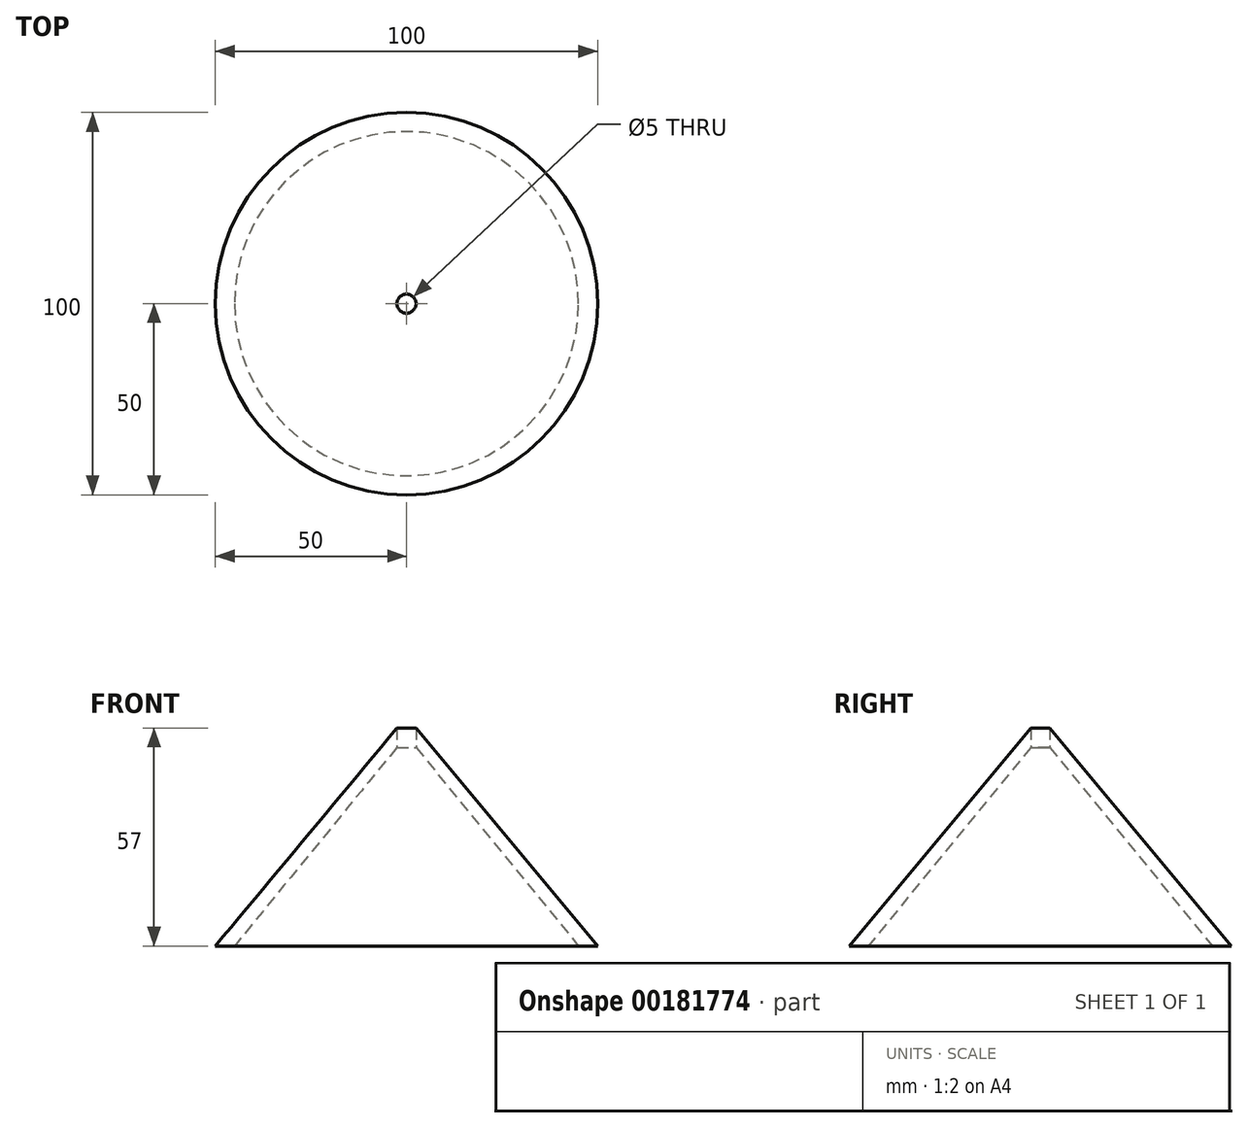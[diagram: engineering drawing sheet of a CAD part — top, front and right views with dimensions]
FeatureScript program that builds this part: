
annotation { "Feature Type Name" : "Feature", "Feature Type Description" : "" }
export const myFeature = defineFeature(function(context is Context, id is Id, definition is map)
    precondition{}
    {
        {
            var Q0;
            Q0=qCreatedBy(makeId("Front.planeOp"),FACE);
            var sketch = newSketch(context, id + "F0", { "sketchPlane" : qUnion([Q0])});
            skLineSegment(sketch, "E0", {"start": v(0, 60) * mm, "end": v(0, 0) * mm});
            skLineSegment(sketch, "E1", {"start": v(0, 0) * mm, "end": v(50, 0) * mm});
            skLineSegment(sketch, "E2", {"start": v(50, 0) * mm, "end": v(0, 60) * mm});
            skSolve(sketch);
        }
        {
            var Q0;
            Q0=makeQuery(id+"F0.imprint","IMPRINT",FACE,{"disambiguationData":[TD([[makeQuery(id+"F0.imprint","IMPRINT",EDGE,{"derivedFrom":sQuery(id+"F0.wireOp",EDGE,"E0")}),1.0]])]});
            var Q1;
            Q1=sQuery(id+"F0.wireOp",EDGE,"E0");
            revolve(context, id + "F1", {"entities" : qUnion([Q0]), "axis" : qUnion([Q1]), "revolveType" : RevolveType.FULL});
        }
        {
            var Q0;
            Q0=qCreatedBy(makeId("Top.planeOp"),FACE);
            var sketch = newSketch(context, id + "F2", { "sketchPlane" : qUnion([Q0])});
            skCircle(sketch, "E3", {"center": v(0, 0) * mm, "radius": 2.5 * mm});
            skSolve(sketch);
        }
        {
            var Q0;
            Q0 = qSketchRegion(id + "F2", true);
            extrude(context, id + "F3", {"entities" : qUnion([Q0]), "operationType" : NewBodyOperationType.REMOVE, "depth" : 60 * mm});
        }
        {
            var Q0;
            Q0=qCreatedBy(makeId("Front.planeOp"),FACE);
            var sketch = newSketch(context, id + "F4", { "sketchPlane" : qUnion([Q0])});
            skLineSegment(sketch, "E4", {"start": v(0, 0) * mm, "end": v(0, 55) * mm});
            skLineSegment(sketch, "E5", {"start": v(0, 0) * mm, "end": v(45, 0) * mm});
            skLineSegment(sketch, "E6", {"start": v(0, 55) * mm, "end": v(45, 0) * mm});
            skSolve(sketch);
        }
        {
            var Q0;
            Q0 = qSketchRegion(id + "F4", true);
            var Q1;
            Q1=sQuery(id+"F4.wireOp",EDGE,"E4");
            revolve(context, id + "F5", {"operationType" : NewBodyOperationType.REMOVE, "entities" : qUnion([Q0]), "axis" : qUnion([Q1]), "revolveType" : RevolveType.FULL, "oppositeDirection" : true});
        }
    });
